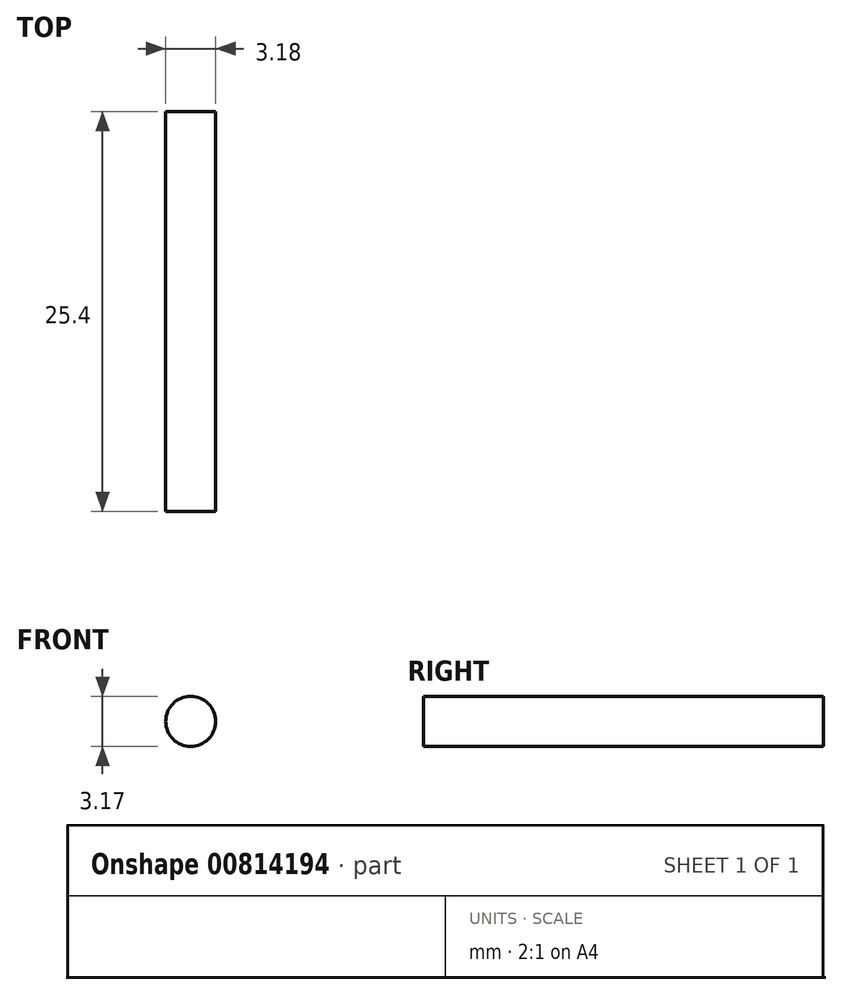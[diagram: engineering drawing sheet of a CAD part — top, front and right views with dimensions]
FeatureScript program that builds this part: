
annotation { "Feature Type Name" : "Feature", "Feature Type Description" : "" }
export const myFeature = defineFeature(function(context is Context, id is Id, definition is map)
    precondition{}
    {
        {
            var Q0;
            Q0=qCreatedBy(makeId("Front.planeOp"),FACE);
            var sketch = newSketch(context, id + "F0", { "sketchPlane" : qUnion([Q0])});
            skCircle(sketch, "E0", {"center": v(-52.27, 43.7) * mm, "radius": 1.59 * mm});
            skSolve(sketch);
        }
        {
            var Q0;
            Q0=makeQuery(id+"F0.imprint","IMPRINT",FACE,{"disambiguationData":[TD([[makeQuery(id+"F0.imprint","IMPRINT",EDGE,{"derivedFrom":sQuery(id+"F0.wireOp",EDGE,"E0")}),1.0]])]});
            extrude(context, id + "F1", {"entities" : qUnion([Q0]), "depth" : 25.4 * mm, "offsetDistance" : 25.4 * mm});
        }
    });
